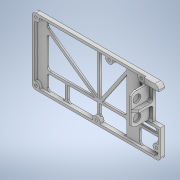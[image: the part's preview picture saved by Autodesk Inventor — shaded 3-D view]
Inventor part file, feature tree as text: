
AUTODESK INVENTOR PART (.ipt)
format: ipt  version: 2021 (Build 250183000, 183)  size: 624,640 bytes
history: native  units: mm
features: sketch x24, extrude x23, fillet x8, hole x1, chamfer x1
ambient origin geometry x8: Origin, YZ Plane, XZ Plane, XY Plane, X Axis, Y Axis, Z Axis, Center Point
bodies: Solid1 (feature_tree)
feature tree (57):
  extrude  "Extrusion1"  Depth=52.0mm
  fillet  "Fillet1"  Radius=2.0mm
  extrude  "Extrusion2"  Depth=2.0mm
  hole  "Hole1"  [1 undecoded]
  extrude  "Extrusion3"  Depth=3.0mm
  extrude  "Extrusion4"  Depth=3.0mm
  fillet  "Fillet2"  Radius=50.0mm
  fillet  "Fillet3"  Radius=8.0mm
  extrude  "Extrusion5"  Depth=3.0mm
  extrude  "Extrusion6"  Depth=49.0mm
  extrude  "Extrusion7"  Depth=49.0mm
  extrude  "Extrusion8"  Depth=6.0mm
  extrude  "Extrusion9"  Depth=6.0mm
  extrude  "Extrusion11"  Depth=6.0mm
  extrude  "Extrusion12"  Depth=24.0mm
  fillet  "Fillet6"  Radius=2.0mm
  fillet  "Fillet7"  Radius=2.0mm
  extrude  "Extrusion13"  Depth=15.0mm
  extrude  "Extrusion14"  Depth=2.0mm
  extrude  "Extrusion15"  Depth=2.0mm
  extrude  "Extrusion16"  Depth=1.2mm TaperAngle=0.0deg
  fillet  "Fillet8"  Radius=25.0mm
  extrude  "Extrusion17"  Depth=1.2mm TaperAngle=0.0deg
  extrude  "Extrusion18"  Depth=2.0mm
  extrude  "Extrusion19"  Depth=29.0mm
  extrude  "Extrusion20"  Depth=2.0mm
  extrude  "Extrusion21"  Depth=3.0mm TaperAngle=0.0deg
  extrude  "Extrusion22"  Depth=1.4mm
  fillet  "Fillet9"  Radius=3.0mm
  chamfer  "Chamfer1"  Distance=1.5mm
  fillet  "Fillet10"  Radius=3.0mm
  extrude  "Extrusion23"  Depth=1.0mm
  extrude  "Extrusion24"  Depth=3.0mm
  sketch  "Sketch1"  dims[d0=100.0mm d1=52.0mm d2=2.0mm]
  sketch  "Sketch2"  dims[d3=2.0mm d4=2.0mm]
  sketch  "Sketch3"  dims[d5=2.0mm d6=3.0mm d7=0.0mm]
  sketch  "Sketch4"  dims[d8=3.0mm d9=3.0mm]
  sketch  "Sketch5"  dims[d10=3.0mm d11=3.0mm d12=50.0mm d13=8.0mm]
  sketch  "Sketch6"  dims[d14=97.0mm d15=3.0mm]
  sketch  "Sketch7"  dims[d16=49.0mm d17=60.0mm]
  sketch  "Sketch8"  dims[d18=49.0mm d19=85.0mm]
  sketch  "Sketch9"  dims[d20=49.0mm d21=6.0mm]
  sketch  "Sketch10"  dims[d22=6.0mm d23=6.0mm]
  sketch  "Sketch12"  dims[d24=6.0mm d25=6.0mm]
  sketch  "Sketch13"  dims[d26=3.0mm d27=0.0mm]
  sketch  "Sketch14"  dims[d28=2.0mm d29=6.0mm d30=4.0mm d31=2.0mm d32=90.0deg d33=4.0mm d34=20.594885mm d35=24.0mm d36=2.0mm d37=2.0mm]
  sketch  "Sketch15"  dims[d38=15.0mm d39=15.0mm]
  sketch  "Sketch16"  dims[d40=2.0mm d41=2.0mm]
  sketch  "Sketch17"  dims[d42=2.0mm d43=2.0mm]
  sketch  "Sketch18"  dims[d44=2.0mm d45=1.2mm d46=0.0mm d47=25.0mm]
  sketch  "Sketch19"  dims[d48=2.0mm d49=1.2mm d50=0.0mm]
  sketch  "Sketch20"  dims[d51=2.0mm d52=2.0mm]
  sketch  "Sketch21"  dims[d53=12.0mm d54=29.0mm]
  sketch  "Sketch22"  dims[d55=10.0mm d56=0.0mm d57=2.0mm]
  sketch  "Sketch23"  dims[d58=2.0mm d59=3.0mm d60=0.0mm]
  sketch  "Sketch24"  dims[d62=1.4mm d63=1.4mm d64=3.0mm d65=1.5mm d66=0.0mm d67=3.0mm]
  sketch  "Sketch25"  dims[d68=1.0mm d69=1.0mm d70=3.0mm d71=2.0mm d72=0.0mm d73=3.0mm d74=1.5mm d75=0.0mm d79=10.0mm d80=18.0mm d81=1.0mm d82=1.0mm d83=3.0mm d84=1.2mm d85=0.0mm d86=41.096396mm d87=10.0mm d88=5.0mm d89=5.0mm d90=3.0mm d91=0.8mm d92=4.5mm d93=1.2mm d94=0.0mm d95=2.0mm d96=2.0mm d97=5.0mm d98=0.0mm d99=2.0mm d100=3.0mm d101=0.0mm d102=0.2mm d103=1.5mm d104=0.0mm d105=4.0mm d106=4.5mm d107=0.0mm d108=3.0mm d109=12.0mm d110=0.0mm d111=0.3mm d112=12.0mm d113=0.0mm d114=6.0mm d115=6.0mm d116=7.0mm d117=7.0mm d118=29.0mm d119=42.0mm d120=12.0mm d121=0.0mm d122=11.0mm d123=11.0mm d124=0.3mm d125=0.2mm d126=2.0mm d127=0.0mm d128=0.6mm d129=2.0mm d130=0.0mm d131=2.0mm d132=11.0mm d133=11.0mm d134=2.0mm d135=3.0mm d136=0.0mm d137=2.0mm d138=3.0mm d139=2.0mm d140=45.0deg d141=2.0mm d142=1.5mm d143=0.0mm d144=1.0mm d145=1.0mm d146=3.0mm d147=0.0mm d76=0.872665mm]
note: 1 required parameter value undecoded (feature->parameter linkage not recoverable at this tier; creation-order binding heuristic only, values carry confidence <= 0.55)
